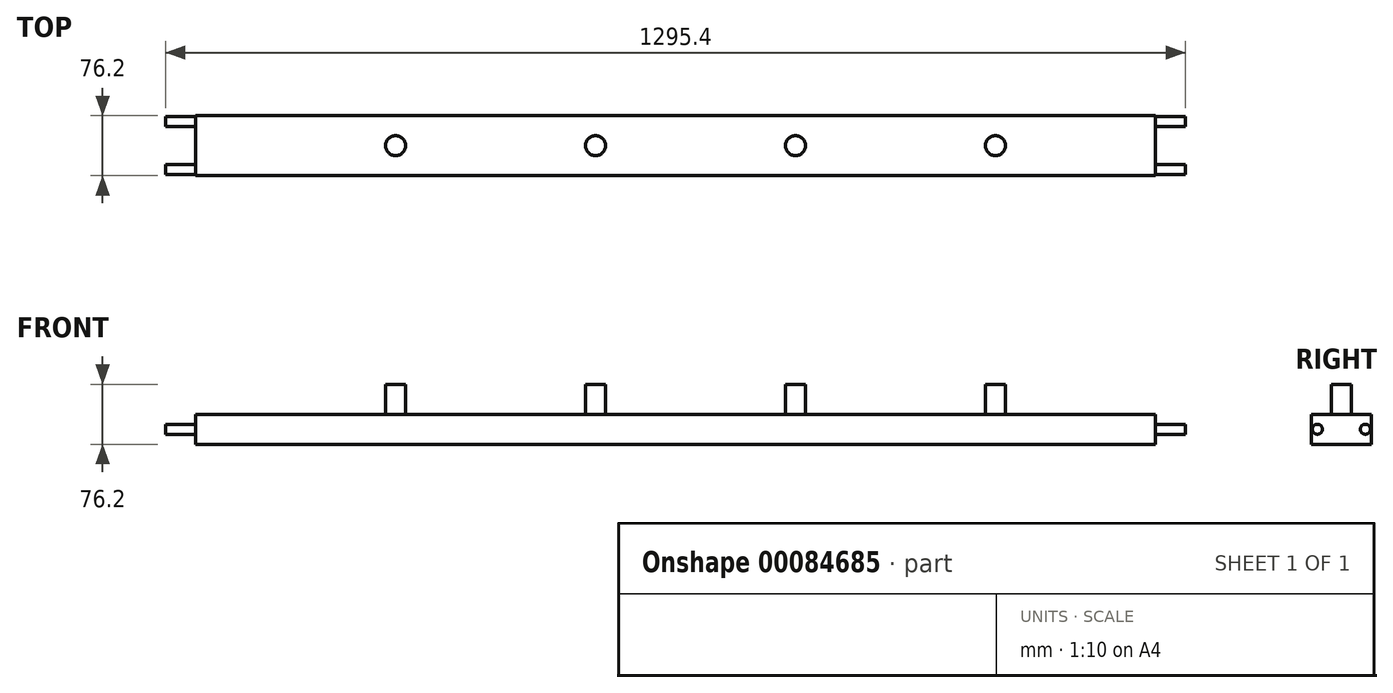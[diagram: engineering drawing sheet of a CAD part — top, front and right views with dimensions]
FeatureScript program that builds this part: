
annotation { "Feature Type Name" : "Feature", "Feature Type Description" : "" }
export const myFeature = defineFeature(function(context is Context, id is Id, definition is map)
    precondition{}
    {
        {
            var Q0;
            Q0=qCreatedBy(makeId("Top.planeOp"),FACE);
            var sketch = newSketch(context, id + "F0", { "sketchPlane" : qUnion([Q0])});
            skLineSegment(sketch, "E0.bottom", {"start": v(-144.87, 28.07) * mm, "end": v(1074.33, 28.07) * mm});
            skLineSegment(sketch, "E0.top", {"start": v(-144.87, -48.13) * mm, "end": v(1074.33, -48.13) * mm});
            skLineSegment(sketch, "E0.left", {"start": v(-144.87, 28.07) * mm, "end": v(-144.87, -48.13) * mm});
            skLineSegment(sketch, "E0.right", {"start": v(1074.33, 28.07) * mm, "end": v(1074.33, -48.13) * mm});
            skSolve(sketch);
        }
        {
            var Q0;
            Q0 = qSketchRegion(id + "F0", true);
            extrude(context, id + "F1", {"entities" : qUnion([Q0]), "depth" : 38.1 * mm});
        }
        {
            var Q0;
            Q0=makeQuery(id+"F1.opExtrude","CAP_FACE",FACE,{"disambiguationData":[OSD([sQuery(id+"F0.wireOp",EDGE,"E0.bottom"),sQuery(id+"F0.wireOp",EDGE,"E0.top"),sQuery(id+"F0.wireOp",EDGE,"E0.left"),sQuery(id+"F0.wireOp",EDGE,"E0.right")])],"isStart":false});
            var sketch = newSketch(context, id + "F2", { "sketchPlane" : qUnion([Q0])});
            skLineSegment(sketch, "E1", {"start": v(-144.87, -10.03) * mm, "end": v(1074.33, -10.03) * mm, "construction": true});
            skCircle(sketch, "E2", {"center": v(109.13, -10.03) * mm, "radius": 12.7 * mm});
            skCircle(sketch, "E3", {"center": v(363.13, -10.03) * mm, "radius": 12.7 * mm});
            skCircle(sketch, "E4", {"center": v(617.13, -10.03) * mm, "radius": 12.7 * mm});
            skCircle(sketch, "E5", {"center": v(871.13, -10.03) * mm, "radius": 12.7 * mm});
            skSolve(sketch);
        }
        {
            var Q0;
            Q0 = qSketchRegion(id + "F2", true);
            extrude(context, id + "F3", {"entities" : qUnion([Q0]), "operationType" : NewBodyOperationType.ADD, "depth" : 38.1 * mm});
        }
        {
            var Q0;
            Q0=makeQuery(id+"F1.opExtrude","SWEPT_FACE",FACE,{"disambiguationData":[OSD([sQuery(id+"F0.wireOp",EDGE,"E0.left")])]});
            var sketch = newSketch(context, id + "F4", { "sketchPlane" : qUnion([Q0])});
            skLineSegment(sketch, "E6", {"start": v(-28.07, 19.05) * mm, "end": v(48.13, 19.05) * mm});
            skLineSegment(sketch, "E7", {"start": v(10.03, 38.1) * mm, "end": v(10.03, 0) * mm});
            skCircle(sketch, "E8", {"center": v(-20.45, 19.05) * mm, "radius": 6.35 * mm});
            skCircle(sketch, "E9", {"center": v(40.5, 19.05) * mm, "radius": 6.35 * mm});
            skSolve(sketch);
        }
        {
            var Q0;
            Q0 = qSketchRegion(id + "F4", true);
            extrude(context, id + "F5", {"entities" : qUnion([Q0]), "operationType" : NewBodyOperationType.ADD, "depth" : 38.1 * mm});
        }
        {
            var Q0;
            Q0=makeQuery(id+"F1.opExtrude","SWEPT_FACE",FACE,{"disambiguationData":[OSD([sQuery(id+"F0.wireOp",EDGE,"E0.right")])]});
            var sketch = newSketch(context, id + "F6", { "sketchPlane" : qUnion([Q0])});
            skLineSegment(sketch, "E10", {"start": v(-48.13, 19.05) * mm, "end": v(28.07, 19.05) * mm});
            skCircle(sketch, "E11", {"center": v(-40.5, 19.05) * mm, "radius": 6.35 * mm});
            skCircle(sketch, "E12", {"center": v(20.45, 19.05) * mm, "radius": 6.35 * mm});
            skSolve(sketch);
        }
        {
            var Q0;
            Q0 = qSketchRegion(id + "F6", true);
            extrude(context, id + "F7", {"entities" : qUnion([Q0]), "operationType" : NewBodyOperationType.ADD, "depth" : 38.1 * mm});
        }
    });
